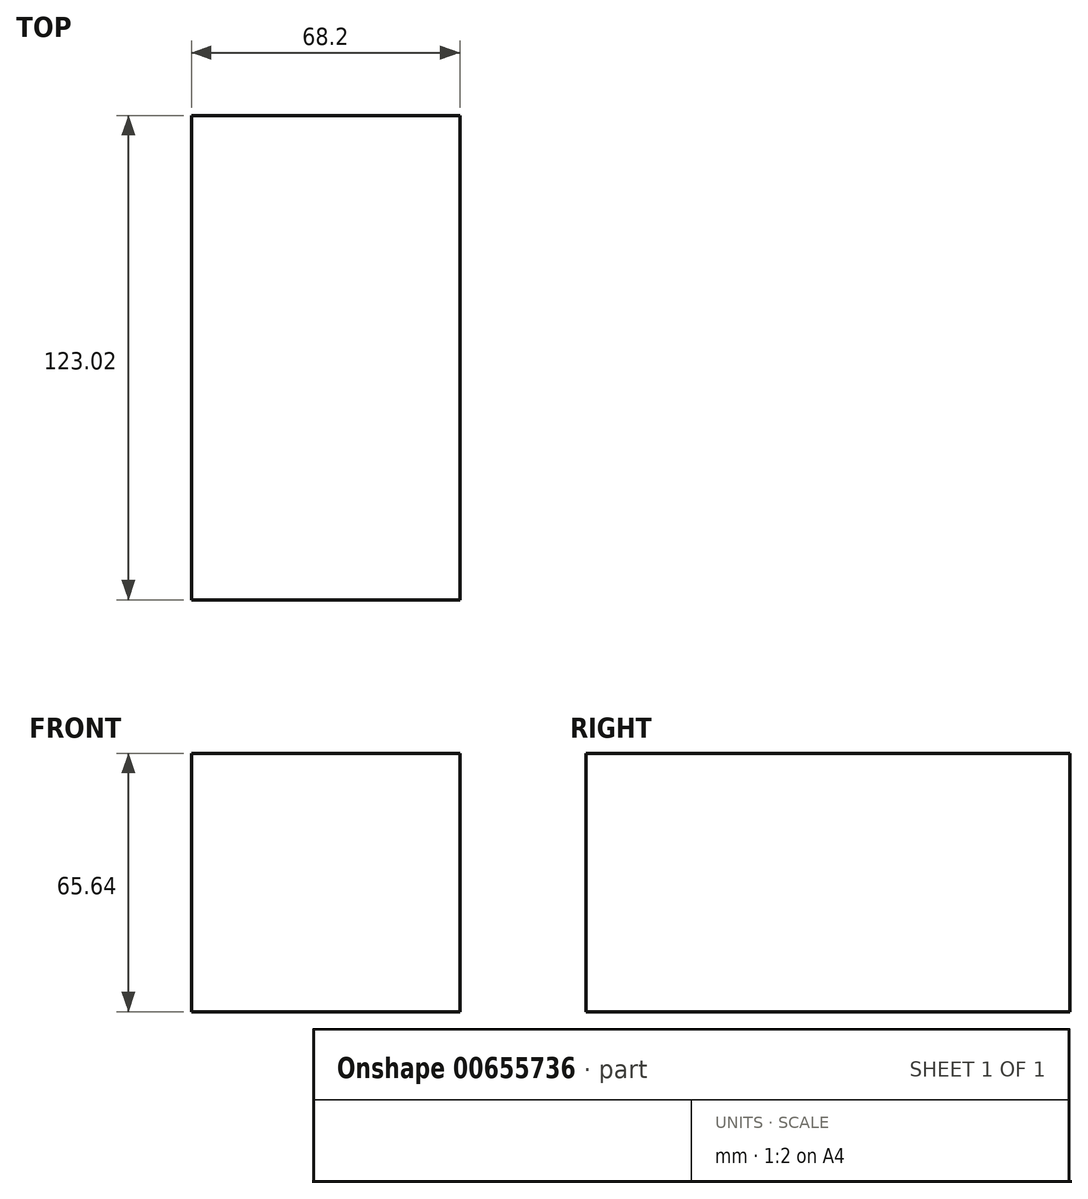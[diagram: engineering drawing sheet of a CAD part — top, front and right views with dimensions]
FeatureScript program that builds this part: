
annotation { "Feature Type Name" : "Feature", "Feature Type Description" : "" }
export const myFeature = defineFeature(function(context is Context, id is Id, definition is map)
    precondition{}
    {
        {
            var Q0;
            Q0=qCreatedBy(makeId("Front.planeOp"),FACE);
            var sketch = newSketch(context, id + "F0", { "sketchPlane" : qUnion([Q0])});
            skLineSegment(sketch, "E0.bottom", {"start": v(-35.38, 33.25) * mm, "end": v(32.82, 33.25) * mm});
            skLineSegment(sketch, "E0.top", {"start": v(-35.38, -32.4) * mm, "end": v(32.82, -32.4) * mm});
            skLineSegment(sketch, "E0.left", {"start": v(-35.38, 33.25) * mm, "end": v(-35.38, -32.4) * mm});
            skLineSegment(sketch, "E0.right", {"start": v(32.82, 33.25) * mm, "end": v(32.82, -32.4) * mm});
            skSolve(sketch);
        }
        {
            var Q0;
            Q0=makeQuery(id+"F0.imprint","IMPRINT",FACE,{"disambiguationData":[TD([[makeQuery(id+"F0.imprint","IMPRINT",EDGE,{"derivedFrom":sQuery(id+"F0.wireOp",EDGE,"E0.bottom")}),-1.0]])]});
            extrude(context, id + "F1", {"entities" : qUnion([Q0]), "depth" : 123.02 * mm, "offsetDistance" : 25 * mm});
        }
    });
